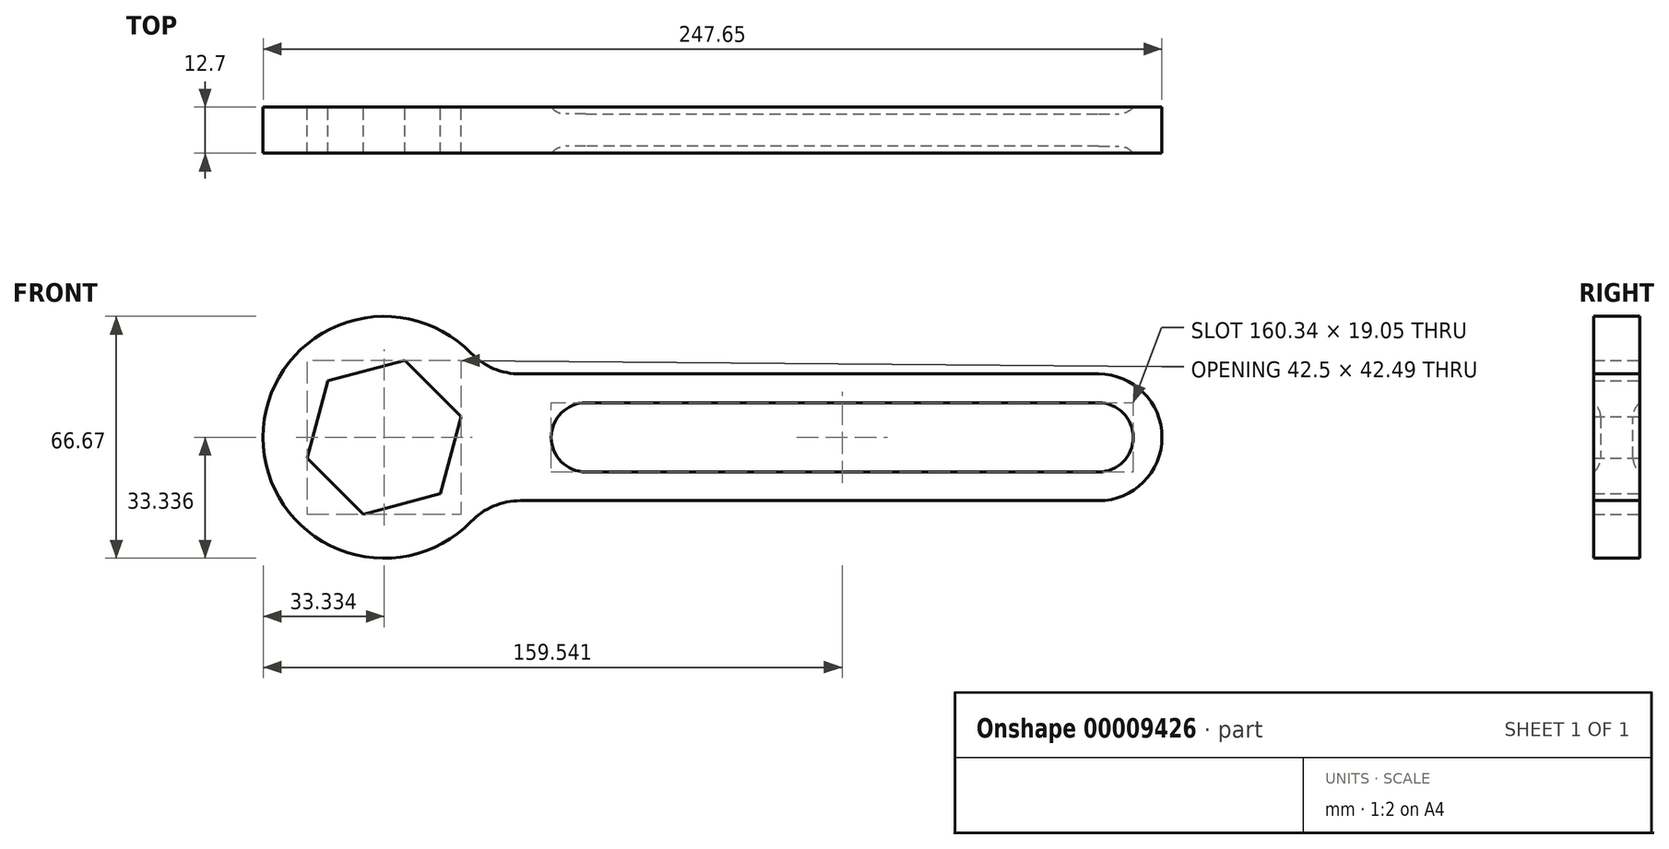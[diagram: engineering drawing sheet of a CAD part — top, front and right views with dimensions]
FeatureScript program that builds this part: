
annotation { "Feature Type Name" : "Feature", "Feature Type Description" : "" }
export const myFeature = defineFeature(function(context is Context, id is Id, definition is map)
    precondition{}
    {
        {
            var Q0;
            Q0=qCreatedBy(makeId("Front.planeOp"),FACE);
            var sketch = newSketch(context, id + "F0", { "sketchPlane" : qUnion([Q0])});
            skLineSegment(sketch, "E0", {"start": v(-116.76, 78.97) * mm, "end": v(-116.76, -79.46) * mm, "construction": true});
            skLineSegment(sketch, "E1", {"start": v(80.1, 78.97) * mm, "end": v(80.1, -79.46) * mm, "construction": true});
            skLineSegment(sketch, "E2", {"start": v(-116.76, -0.24) * mm, "end": v(80.1, -0.24) * mm, "construction": true});
            skArc(sketch, "E3", {"start": v(-92.85, 23) * mm, "mid": v(-150.1, -0.24) * mm, "end": v(-92.85, -23.48) * mm});
            skArc(sketch, "E4", {"start": v(80.1, -17.7) * mm, "mid": v(97.56, -0.24) * mm, "end": v(80.1, 17.22) * mm});
            skLineSegment(sketch, "E5", {"start": v(80.1, 17.22) * mm, "end": v(-79.19, 17.22) * mm});
            skLineSegment(sketch, "E6", {"start": v(80.1, -17.7) * mm, "end": v(-79.19, -17.7) * mm});
            skPoint(sketch, "E7.visualSharp", {"position": v(-88.36, 17.22) * mm});
            skArc(sketch, "E7.filletArc", {"start": v(-92.85, 23) * mm, "mid": v(-86.6, 18.72) * mm, "end": v(-79.19, 17.22) * mm});
            skPoint(sketch, "E8.visualSharp", {"position": v(-88.36, -17.7) * mm});
            skArc(sketch, "E8.filletArc", {"start": v(-79.19, -17.7) * mm, "mid": v(-86.6, -19.2) * mm, "end": v(-92.85, -23.48) * mm});
            skArc(sketch, "E9", {"start": v(-92.85, -23.48) * mm, "mid": v(-83.42, -0.24) * mm, "end": v(-92.85, 23) * mm});
            skArc(sketch, "E10", {"start": v(80.1, -9.77) * mm, "mid": v(89.62, -0.24) * mm, "end": v(80.1, 9.28) * mm});
            skLineSegment(sketch, "E11", {"start": v(-61.2, -0.24) * mm, "end": v(-61.2, -53.22) * mm, "construction": true});
            skArc(sketch, "E12", {"start": v(-61.2, 9.28) * mm, "mid": v(-70.72, -0.24) * mm, "end": v(-61.2, -9.77) * mm});
            skLineSegment(sketch, "E13", {"start": v(-61.2, 9.28) * mm, "end": v(80.1, 9.28) * mm});
            skLineSegment(sketch, "E14", {"start": v(-61.2, -9.77) * mm, "end": v(80.1, -9.77) * mm});
            skCircle(sketch, "E15.cCircle", {"center": v(-116.76, -0.24) * mm, "radius": 19.05 * mm, "construction": true});
            skLineSegment(sketch, "E15.0", {"start": v(-132.3, 15.31) * mm, "end": v(-111.06, 21) * mm});
            skLineSegment(sketch, "E15.1", {"start": v(-111.06, 21) * mm, "end": v(-95.5, 5.45) * mm});
            skLineSegment(sketch, "E15.2", {"start": v(-95.5, 5.45) * mm, "end": v(-101.2, -15.8) * mm});
            skLineSegment(sketch, "E15.3", {"start": v(-101.2, -15.8) * mm, "end": v(-122.45, -21.5) * mm});
            skLineSegment(sketch, "E15.4", {"start": v(-122.45, -21.5) * mm, "end": v(-138, -5.94) * mm});
            skLineSegment(sketch, "E15.5", {"start": v(-138, -5.94) * mm, "end": v(-132.3, 15.31) * mm});
            skPoint(sketch, "E15.0.midPoint", {"position": v(-121.69, 18.16) * mm});
            skLineSegment(sketch, "E16", {"start": v(-122.45, -21.5) * mm, "end": v(-176.76, -36.04) * mm, "construction": true});
            skSolve(sketch);
        }
        {
            var Q0;
            Q0=makeQuery(id+"F0.imprint","IMPRINT",FACE,{"disambiguationData":[TD([[makeQuery(id+"F0.imprint","IMPRINT",EDGE,{"derivedFrom":sQuery(id+"F0.wireOp",EDGE,"E4")}),1.0]])]});
            var Q1;
            Q1=makeQuery(id+"F0.imprint","IMPRINT",FACE,{"disambiguationData":[TD([[makeQuery(id+"F0.imprint","IMPRINT",EDGE,{"derivedFrom":sQuery(id+"F0.wireOp",EDGE,"E3")}),1.0]])]});
            extrude(context, id + "F1", {"entities" : qUnion([Q0, Q1]), "endBound" : BoundingType.SYMMETRIC, "depth" : 12.7 * mm});
        }
        {
            var Q0;
            Q0=makeQuery(id+"F0.imprint","IMPRINT",FACE,{"disambiguationData":[TD([[makeQuery(id+"F0.imprint","IMPRINT",EDGE,{"derivedFrom":sQuery(id+"F0.wireOp",EDGE,"E10")}),1.0]])]});
            extrude(context, id + "F2", {"entities" : qUnion([Q0]), "operationType" : NewBodyOperationType.ADD, "endBound" : BoundingType.SYMMETRIC, "depth" : 8.9 * mm});
        }
        {
            var Q0;
            Q0=makeQuery(id+"F2.opExtrude","CAP_FACE",FACE,{"disambiguationData":[OSD([sQuery(id+"F0.wireOp",EDGE,"E10"),sQuery(id+"F0.wireOp",EDGE,"E12"),sQuery(id+"F0.wireOp",EDGE,"E13"),sQuery(id+"F0.wireOp",EDGE,"E14")])],"isStart":false});
            var Q1;
            Q1=makeQuery(id+"F2.opExtrude","CAP_FACE",FACE,{"disambiguationData":[OSD([sQuery(id+"F0.wireOp",EDGE,"E10"),sQuery(id+"F0.wireOp",EDGE,"E12"),sQuery(id+"F0.wireOp",EDGE,"E13"),sQuery(id+"F0.wireOp",EDGE,"E14")])],"isStart":true});
            fillet(context, id + "F3", {"entities" : qUnion([Q0, Q1]), "radius" : 5.08 * mm, "tangentPropagation" : true, "allowEdgeOverflow" : false});
        }
    });
